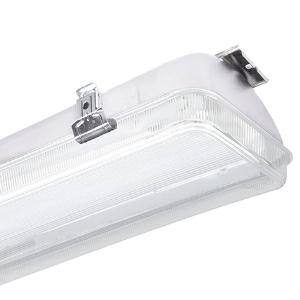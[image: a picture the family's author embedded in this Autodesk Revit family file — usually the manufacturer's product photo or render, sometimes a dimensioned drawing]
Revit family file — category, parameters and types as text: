
# Revit family: 3f_filippi_-_beta_235_75_pc_ampio_3f_filippi_-_52849_-_beta_235_led_751x50_ampio_l1265
name_source: partatom
category: Lighting Fixtures
units: mm (PartAtom-declared; Revit-internal decimal feet)

## family parameters
Cut with Voids When Loaded = No
Host = Face
Light Source = No
Part Type = Normal
Room Calculation Point = No
Round Connector Dimension = Use Diameter
Shared = No

## types (1)
- 3F Filippi - Beta 235 75 PC Ampio (1 x LED, 8174 lm, 54 W, 4000 K)
    Apparent Load = 54 VA
    Approval mark = CE
    CIE Flux Codes = 60 88 98 97 100
    Color Rendering = 80
    Color Temperature = 4000 K
    Control Gear = Electronic ballast
    Default Elevation = 1800 mm
    Description = ILLUMINOTECHNICAL
Luminous efficiency 100% (DLOR 99%, ULOR 1%).
Initial luminous flux of the luminaire 8174 lm.
Wide symmetric distribution.
Installation Interdistance Transv.D = 1.25 x hu - Long.D = 1.44 x hu.
Tabular UGR (CIE 117 - 4H-8H; S=0.25H; 70/50/20): RUG 19.4 - 19.9.
Beam angle: 91° - 102°.
Luminous efficacy 151 lm/W.
Lifetime (L93/B10): 30000 h. (tq+25°C)
Lifetime (L90/B10): 50000 h. (tq+25°C)
Lifetime (L85/B10): 80000 h. (tq+25°C)
Lifetime (L80/B10): 100000 h. (tq+25°C)
Lifetime (L85/B10): 50000 h. (tq+45°C)
Sudden decreased luminous flux after 50000 hours: 0% (C0).
Photobiological safety in compliance with IEC/TR 62778: RG0 risk exempt, (IEC 62471).
In compliance with IEC/EN 62722-2-1 - IEC/EN 62717 standards.

SOURCE
Linear LED module 50W/840.
Energy efficiency class (UE 2019/2020 - UE 2019/2015): C.
CIE 13.3 Colour rendering index: CRI >80 (R9 <50%).
IES TM-30 Fidelity Index: Rf = 84 Rg = 95.
CCT nominal colour temperature 4000 K.
Colour initial tolerance (MacAdam): SDCM 3.

MECHANICAL
Single-piece housing in pressed steel, powder-coated in white epoxy-polyester.
Polycarbonate screen etched internally, V2 self-extinguishing, UV stabilised, injection moulded.
Ecologic anti-aging injected sealing gasket.
Oversized gear-tray reflector unit in highly reflective white painted hot-galvanised steel.
Methacrylate (PMMA) lenses with external flat surface.
Galvanised steel snap-lock clips for diffuser mounting (safety n° 4 per fixture).
Luminaire with limited surface temperature. - D - (EN 60598-2-24)
Dimensions: 1265x235 mm, height 135 mm. Weight 6.85 kg.
IP65 protection degree.
Mechanical strength to impacts IK10 (20 joule).
Glow-wire test resistance 850°C.

ELECTRICAL
Halogen Free electronic wiring 230V-50/60Hz, power factor 0.95, THD <25%, constant output current, class I, 1 driver.
Power of the luminaire 54 W.
ENEC - CE.
Flicker: <4%.
Luminaire compliant with EN 60598-2-22 for power supply from a centralised emergency system CPSS (Central Power Supply System), not incorporated in the luminaire - high risk areas excluded. The default power and flux are 100% in AC and 100% in DC.
Ambient temperature from -20°C to +45°C.
Temperature class T6 max 85°C.
Quick connection via M20 3P connector with 9-13 mm tightening range.
Relative humidity UR: <85%.

INSTALLATION
Ceiling / Suspended / Wall.
All accessories dedicated to this product are available on the Catalog and on our website www.3F-Filippi.com.

APPLICATIONS
Suitable product for food production plants (HACCP), IFS (Food Version 6), BRC (GSFS Food Version 7).
Dry, dusty indoor environments, subject to occasional water splashes.
Industrial environments, warehouses, environments where security locks are required on all clips, e.g. prisons (on request).
Environments in which it is necessary a total protection against falling fragments (eg environments with foodstuffs or machines with moving parts or with extreme temperature changes), use luminaires with laminated glass.
Tempered glass is not immune to falling fragments from harmless and caused by shocks or exceptionally derived from the tempering process.

WARNING
Fixture not suitable for cold stores with an ambient temperature <0°C and/or relative humidity >85%.
Luminaire designed for disposal/recycling at end-of-life.
Replaceable (LED only) light source by a professional. Replaceable control gear by a professional.
    Height = 135 mm
    Lamp = 1 x LED
    Lamp Light Flux = 8174 lm
    Lamp Power = 54 W
    Lamp count = 1
    Length = 1265 mm
    Lifetime = 50000 h
    Luminous efficacy = 151 lm/W
    Manufacturer = 3F Filippi
    ModVariant = No
    Model = 3F Filippi - 52849 - Beta 235 LED 751x50 AMPIO L1265
    Mounting Place = Ceiling
    Mounting Type = Pendant
    Number of Poles = 1
    OnlyDefault = Yes
    Power Factor = 1
    Product Name = 3F Filippi - Beta 235 75 PC Ampio
    Product group = pendant luminaire
    ProductGroupID = 9
    Protection Class = Protection class I
    Protection Degree = IP 65
    RLX_Detail_Level = 1
    RLX_Emergency_Light_Flux = 0 lm
    RLX_Emergency_Type = 0
    RLX_Emergency_Type_DB = No
    RlxData = <blob elided: 90189 chars, md5=2a1122b5>
    Socket = socket
    Standby Power = 0 W
    System Light Flux = 8174 lm
    System Power = 54 W
    Type Comments = Product without accessories
    Type Image = 3ffilippi_52849.jpg
    URL = http://relux.com
    VarID = ---
    Voltage = 0 V
    Weight = 0.00 kg
    Width = 235 mm

## geometry (parser evidence)
native form markers: Blend x4, Sweep x11
no freeform markers — native parametric forms only
